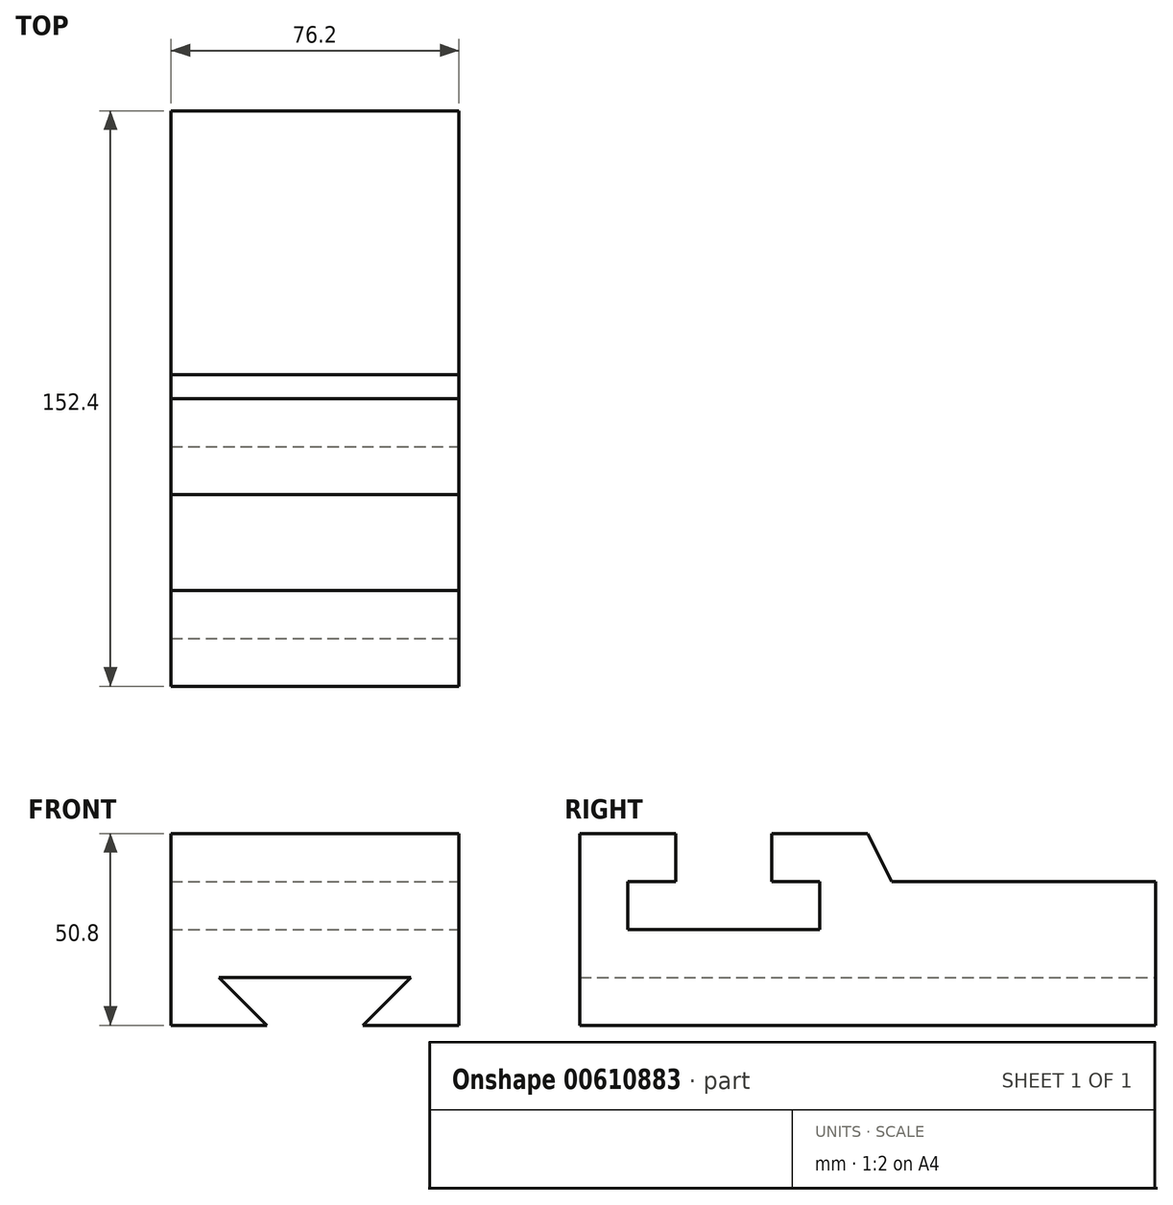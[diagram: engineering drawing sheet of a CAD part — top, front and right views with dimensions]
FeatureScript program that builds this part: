
annotation { "Feature Type Name" : "Feature", "Feature Type Description" : "" }
export const myFeature = defineFeature(function(context is Context, id is Id, definition is map)
    precondition{}
    {
        {
            var Q0;
            Q0=qCreatedBy(makeId("Front.planeOp"),FACE);
            var sketch = newSketch(context, id + "F0", { "sketchPlane" : qUnion([Q0])});
            skLineSegment(sketch, "E0.bottom", {"start": v(0, 0) * mm, "end": v(76.2, 0) * mm});
            skLineSegment(sketch, "E0.top", {"start": v(0, 50.8) * mm, "end": v(76.2, 50.8) * mm});
            skLineSegment(sketch, "E0.left", {"start": v(0, 0) * mm, "end": v(0, 50.8) * mm});
            skLineSegment(sketch, "E0.right", {"start": v(76.2, 0) * mm, "end": v(76.2, 50.8) * mm});
            skSolve(sketch);
        }
        {
            var Q0;
            Q0=makeQuery(id+"F0.imprint","IMPRINT",FACE,{"disambiguationData":[TD([[makeQuery(id+"F0.imprint","IMPRINT",EDGE,{"derivedFrom":sQuery(id+"F0.wireOp",EDGE,"E0.bottom")}),1.0]])]});
            extrude(context, id + "F1", {"entities" : qUnion([Q0]), "oppositeDirection" : true, "depth" : 152.4 * mm, "offsetDistance" : 25.4 * mm});
        }
        {
            var Q0;
            Q0=makeQuery(id+"F1.opExtrude","SWEPT_FACE",FACE,{"disambiguationData":[OSD([sQuery(id+"F0.wireOp",EDGE,"E0.right")])]});
            var sketch = newSketch(context, id + "F2", { "sketchPlane" : qUnion([Q0])});
            skLineSegment(sketch, "E1", {"start": v(25.4, 50.8) * mm, "end": v(25.4, 38.1) * mm});
            skLineSegment(sketch, "E2", {"start": v(25.4, 38.1) * mm, "end": v(12.7, 38.1) * mm});
            skLineSegment(sketch, "E3", {"start": v(12.7, 38.1) * mm, "end": v(12.7, 25.4) * mm});
            skLineSegment(sketch, "E4", {"start": v(12.7, 25.4) * mm, "end": v(63.5, 25.4) * mm});
            skLineSegment(sketch, "E5", {"start": v(63.5, 25.4) * mm, "end": v(63.5, 38.1) * mm});
            skLineSegment(sketch, "E6", {"start": v(63.5, 38.1) * mm, "end": v(50.8, 38.1) * mm});
            skLineSegment(sketch, "E7", {"start": v(50.8, 38.1) * mm, "end": v(50.8, 50.8) * mm});
            skSolve(sketch);
        }
        {
            var Q0;
            {var subQ0=sQuery(id+"F2.wireOp",EDGE,"E1");Q0=makeQuery(id+"F2.imprint","IMPRINT",FACE,{"disambiguationData":[TD([[makeQuery(id+"F2.imprint","IMPRINT",EDGE,{"derivedFrom":subQ0}),1.0]])]});}
            extrude(context, id + "F3", {"entities" : qUnion([Q0]), "operationType" : NewBodyOperationType.REMOVE, "oppositeDirection" : true, "depth" : 76.2 * mm, "offsetDistance" : 25.4 * mm});
        }
        {
            var Q0;
            Q0=makeQuery(id+"F1.opExtrude","SWEPT_FACE",FACE,{"disambiguationData":[OSD([sQuery(id+"F0.wireOp",EDGE,"E0.right")])]});
            var sketch = newSketch(context, id + "F4", { "sketchPlane" : qUnion([Q0])});
            skLineSegment(sketch, "E8.bottom", {"start": v(152.4, 50.8) * mm, "end": v(82.55, 50.8) * mm});
            skLineSegment(sketch, "E8.top", {"start": v(152.4, 38.1) * mm, "end": v(82.55, 38.1) * mm});
            skLineSegment(sketch, "E8.left", {"start": v(152.4, 50.8) * mm, "end": v(152.4, 38.1) * mm});
            skLineSegment(sketch, "E8.right", {"start": v(82.55, 50.8) * mm, "end": v(82.55, 38.1) * mm});
            skLineSegment(sketch, "E9", {"start": v(82.55, 38.1) * mm, "end": v(76.2, 50.8) * mm});
            skSolve(sketch);
        }
        {
            var Q0;
            {var subQ0=sQuery(id+"F4.wireOp",EDGE,"E8.right");Q0=makeQuery(id+"F4.imprint","IMPRINT",FACE,{"disambiguationData":[TD([[makeQuery(id+"F4.imprint","IMPRINT",EDGE,{"derivedFrom":subQ0}),-1.0]])]});}
            var Q1;
            Q1=makeQuery(id+"F4.imprint","IMPRINT",FACE,{"disambiguationData":[TD([[makeQuery(id+"F4.imprint","IMPRINT",EDGE,{"derivedFrom":sQuery(id+"F4.wireOp",EDGE,"E8.bottom")}),1.0]])]});
            extrude(context, id + "F5", {"entities" : qUnion([Q0, Q1]), "operationType" : NewBodyOperationType.REMOVE, "oppositeDirection" : true, "depth" : 76.2 * mm, "offsetDistance" : 25.4 * mm});
        }
        {
            var Q0;
            Q0=makeQuery(id+"F1.opExtrude","CAP_FACE",FACE,{"disambiguationData":[OSD([sQuery(id+"F0.wireOp",EDGE,"E0.bottom"),sQuery(id+"F0.wireOp",EDGE,"E0.top"),sQuery(id+"F0.wireOp",EDGE,"E0.left"),sQuery(id+"F0.wireOp",EDGE,"E0.right")])],"isStart":false});
            var sketch = newSketch(context, id + "F6", { "sketchPlane" : qUnion([Q0])});
            skLineSegment(sketch, "E10", {"start": v(-50.8, 0) * mm, "end": v(-63.5, 12.7) * mm});
            skLineSegment(sketch, "E11", {"start": v(-63.5, 12.7) * mm, "end": v(-12.7, 12.7) * mm});
            skLineSegment(sketch, "E12", {"start": v(-12.7, 12.7) * mm, "end": v(-25.4, 0) * mm});
            skSolve(sketch);
        }
        {
            var Q0;
            {var subQ0=sQuery(id+"F6.wireOp",EDGE,"E10");Q0=makeQuery(id+"F6.imprint","IMPRINT",FACE,{"disambiguationData":[TD([[makeQuery(id+"F6.imprint","IMPRINT",EDGE,{"derivedFrom":subQ0}),-1.0]])]});}
            extrude(context, id + "F7", {"entities" : qUnion([Q0]), "operationType" : NewBodyOperationType.REMOVE, "oppositeDirection" : true, "depth" : 152.4 * mm, "offsetDistance" : 25.4 * mm});
        }
    });
